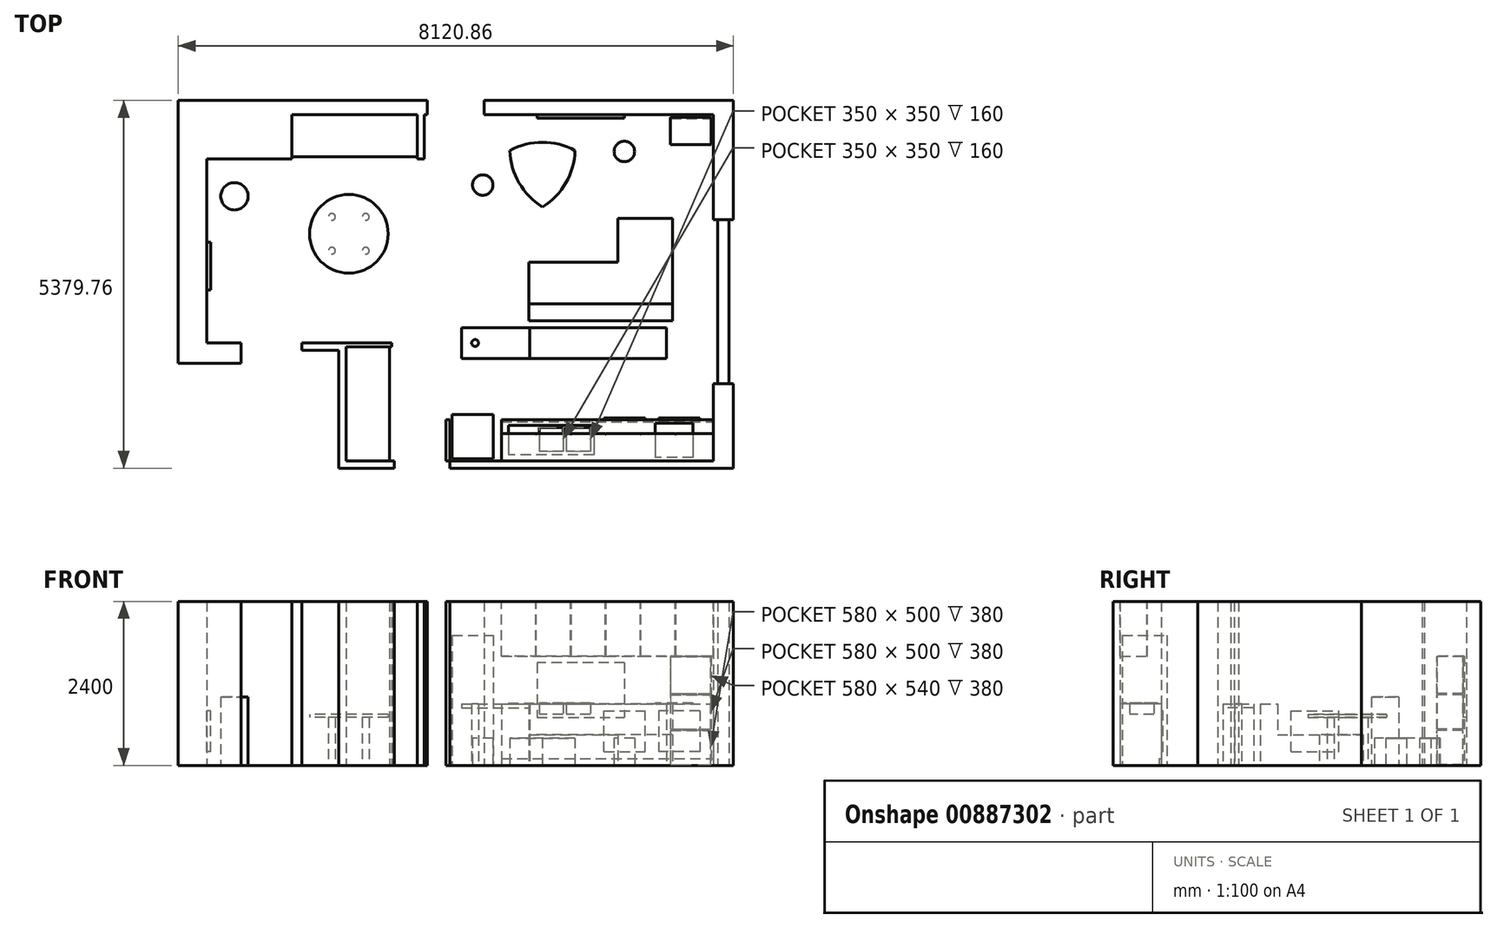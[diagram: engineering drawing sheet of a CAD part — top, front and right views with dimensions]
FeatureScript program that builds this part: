
annotation { "Feature Type Name" : "Feature", "Feature Type Description" : "" }
export const myFeature = defineFeature(function(context is Context, id is Id, definition is map)
    precondition{}
    {
        {
            var Q0;
            Q0=qCreatedBy(makeId("Top.planeOp"),FACE);
            var sketch = newSketch(context, id + "F0", { "sketchPlane" : qUnion([Q0])});
            skLineSegment(sketch, "E0", {"start": v(5332.87, -822.17) * mm, "end": v(1474.75, -822.17) * mm});
            skLineSegment(sketch, "E1", {"start": v(1474.75, -822.17) * mm, "end": v(1474.75, -222.17) * mm});
            skLineSegment(sketch, "E2", {"start": v(1474.75, -222.17) * mm, "end": v(1421.4, -222.17) * mm});
            skLineSegment(sketch, "E3", {"start": v(1421.4, -222.17) * mm, "end": v(1421.4, -822.17) * mm});
            skLineSegment(sketch, "E4", {"start": v(1421.4, -822.17) * mm, "end": v(1474.75, -822.17) * mm});
            skLineSegment(sketch, "E5", {"start": v(5332.87, 309.99) * mm, "end": v(5394.44, 309.99) * mm});
            skLineSegment(sketch, "E6", {"start": v(5394.44, 309.99) * mm, "end": v(5394.44, 2704.75) * mm});
            skLineSegment(sketch, "E7", {"start": v(5394.44, 2704.75) * mm, "end": v(5332.87, 2704.75) * mm});
            skLineSegment(sketch, "E8", {"start": v(5332.87, 2704.75) * mm, "end": v(5332.87, 4243.63) * mm});
            skLineSegment(sketch, "E9", {"start": v(5332.87, 4243.63) * mm, "end": v(1981.19, 4243.63) * mm});
            skLineSegment(sketch, "E10", {"start": v(1981.19, 4243.63) * mm, "end": v(1981.19, 4451) * mm});
            skLineSegment(sketch, "E11", {"start": v(1981.19, 4451) * mm, "end": v(5626.54, 4451) * mm});
            skLineSegment(sketch, "E12", {"start": v(5626.54, 4451) * mm, "end": v(5626.54, 2704.75) * mm});
            skLineSegment(sketch, "E13", {"start": v(5626.54, 2704.75) * mm, "end": v(5394.44, 2704.75) * mm});
            skLineSegment(sketch, "E14", {"start": v(5394.44, 309.99) * mm, "end": v(5626.54, 309.99) * mm});
            skPoint(sketch, "E14.endSnap0", {"position": v(5363.66, 309.99) * mm});
            skLineSegment(sketch, "E15", {"start": v(5626.54, 309.99) * mm, "end": v(5626.54, -928.77) * mm});
            skLineSegment(sketch, "E16", {"start": v(5626.54, -928.77) * mm, "end": v(1474.75, -928.77) * mm});
            skLineSegment(sketch, "E17", {"start": v(1474.75, -928.77) * mm, "end": v(1474.75, -822.17) * mm});
            skLineSegment(sketch, "E18", {"start": v(5558.56, 2704.75) * mm, "end": v(5558.56, 309.99) * mm});
            skLineSegment(sketch, "E19", {"start": v(-37.13, -822.17) * mm, "end": v(664.8, -822.17) * mm});
            skLineSegment(sketch, "E20", {"start": v(664.8, -822.17) * mm, "end": v(664.8, -928.77) * mm});
            skLineSegment(sketch, "E21", {"start": v(664.8, -928.77) * mm, "end": v(-150.57, -928.77) * mm});
            skLineSegment(sketch, "E22", {"start": v(-150.57, -928.77) * mm, "end": v(-150.57, 905.53) * mm});
            skLineSegment(sketch, "E23", {"start": v(-150.57, 905.53) * mm, "end": v(-37.13, 905.53) * mm});
            skLineSegment(sketch, "E24", {"start": v(-37.13, 905.53) * mm, "end": v(-37.13, -26.35) * mm});
            skLineSegment(sketch, "E25", {"start": v(5332.87, 309.99) * mm, "end": v(5332.87, -822.17) * mm});
            skLineSegment(sketch, "E26", {"start": v(-37.13, 905.53) * mm, "end": v(-37.13, -822.17) * mm});
            skLineSegment(sketch, "E27.bottom", {"start": v(1511.94, -792.17) * mm, "end": v(2111.94, -792.17) * mm});
            skLineSegment(sketch, "E27.left", {"start": v(1511.94, -792.17) * mm, "end": v(1511.94, -142.17) * mm});
            skLineSegment(sketch, "E28", {"start": v(1511.94, -142.17) * mm, "end": v(2111.94, -142.17) * mm});
            skLineSegment(sketch, "E29", {"start": v(2111.94, -142.17) * mm, "end": v(2111.94, -792.17) * mm});
            skLineSegment(sketch, "E30", {"start": v(5332.87, -822.17) * mm, "end": v(2232.87, -822.17) * mm, "construction": true});
            skLineSegment(sketch, "E31", {"start": v(2232.87, -822.17) * mm, "end": v(2232.87, -222.17) * mm});
            skLineSegment(sketch, "E32", {"start": v(5332.87, 309.99) * mm, "end": v(4732.87, 309.99) * mm, "construction": true});
            skLineSegment(sketch, "E33", {"start": v(2232.87, -222.17) * mm, "end": v(4732.87, -222.17) * mm});
            skLineSegment(sketch, "E34", {"start": v(4732.87, -222.17) * mm, "end": v(4732.87, 309.99) * mm, "construction": true});
            skLineSegment(sketch, "E35", {"start": v(1647.48, 677.83) * mm, "end": v(4647.48, 677.83) * mm});
            skLineSegment(sketch, "E36", {"start": v(4647.48, 677.83) * mm, "end": v(4647.48, 1127.83) * mm});
            skLineSegment(sketch, "E37", {"start": v(4647.48, 1127.83) * mm, "end": v(1647.48, 1127.83) * mm});
            skLineSegment(sketch, "E38", {"start": v(1647.48, 1127.83) * mm, "end": v(1647.48, 677.83) * mm, "construction": true});
            skLineSegment(sketch, "E39", {"start": v(4732.87, 1227.83) * mm, "end": v(2632.87, 1227.83) * mm});
            skLineSegment(sketch, "E40", {"start": v(2632.87, 1227.83) * mm, "end": v(2632.87, 2087.83) * mm});
            skLineSegment(sketch, "E41", {"start": v(2632.87, 2087.83) * mm, "end": v(3932.87, 2087.83) * mm});
            skLineSegment(sketch, "E42", {"start": v(4732.87, 1227.83) * mm, "end": v(4732.87, 2727.83) * mm});
            skLineSegment(sketch, "E43", {"start": v(4732.87, 2727.83) * mm, "end": v(3932.87, 2727.83) * mm});
            skLineSegment(sketch, "E44", {"start": v(3932.87, 2727.83) * mm, "end": v(3932.87, 2087.83) * mm});
            skLineSegment(sketch, "E45", {"start": v(4732.87, 1227.83) * mm, "end": v(4732.87, 1477.83) * mm, "construction": true});
            skLineSegment(sketch, "E46", {"start": v(4732.87, 1477.83) * mm, "end": v(2632.87, 1477.83) * mm});
            skLineSegment(sketch, "E47.bottom", {"start": v(5301.08, 4208.55) * mm, "end": v(4701.08, 4208.55) * mm});
            skLineSegment(sketch, "E47.top", {"start": v(5301.08, 3808.55) * mm, "end": v(4701.08, 3808.55) * mm});
            skLineSegment(sketch, "E47.left", {"start": v(5301.08, 4208.55) * mm, "end": v(5301.08, 3808.55) * mm});
            skLineSegment(sketch, "E47.right", {"start": v(4701.08, 4208.55) * mm, "end": v(4701.08, 3808.55) * mm});
            skLineSegment(sketch, "E48", {"start": v(4032.87, 4243.63) * mm, "end": v(4032.87, 4193.63) * mm});
            skLineSegment(sketch, "E49", {"start": v(4032.87, 4193.63) * mm, "end": v(2752.87, 4193.63) * mm});
            skLineSegment(sketch, "E50", {"start": v(2752.87, 4193.63) * mm, "end": v(2752.87, 4243.63) * mm});
            skLineSegment(sketch, "E51", {"start": v(2232.87, -549.5) * mm, "end": v(2332.87, -549.5) * mm, "construction": true});
            skLineSegment(sketch, "E52", {"start": v(2332.87, -302.17) * mm, "end": v(2332.87, -732.17) * mm});
            skLineSegment(sketch, "E53", {"start": v(2332.87, -302.17) * mm, "end": v(3582.87, -302.17) * mm});
            skLineSegment(sketch, "E54", {"start": v(3582.87, -302.17) * mm, "end": v(3582.87, -732.17) * mm});
            skLineSegment(sketch, "E55", {"start": v(3582.87, -732.17) * mm, "end": v(2332.87, -732.17) * mm});
            skLineSegment(sketch, "E56", {"start": v(3582.87, -517.17) * mm, "end": v(3532.87, -517.17) * mm, "construction": true});
            skLineSegment(sketch, "E57", {"start": v(3532.87, -517.17) * mm, "end": v(3182.87, -517.17) * mm, "construction": true});
            skLineSegment(sketch, "E58", {"start": v(3182.87, -517.17) * mm, "end": v(3132.87, -517.17) * mm, "construction": true});
            skLineSegment(sketch, "E59", {"start": v(3132.87, -517.17) * mm, "end": v(2782.87, -517.17) * mm, "construction": true});
            skLineSegment(sketch, "E60", {"start": v(3352.05, -302.17) * mm, "end": v(3352.05, -332.17) * mm, "construction": true});
            skLineSegment(sketch, "E61", {"start": v(3352.05, -332.17) * mm, "end": v(3352.05, -682.17) * mm, "construction": true});
            skLineSegment(sketch, "E62.bottom", {"start": v(3532.87, -332.17) * mm, "end": v(3182.87, -332.17) * mm});
            skLineSegment(sketch, "E62.top", {"start": v(3532.87, -682.17) * mm, "end": v(3182.87, -682.17) * mm});
            skLineSegment(sketch, "E62.left", {"start": v(3532.87, -332.17) * mm, "end": v(3532.87, -682.17) * mm});
            skLineSegment(sketch, "E62.right", {"start": v(3182.87, -332.17) * mm, "end": v(3182.87, -682.17) * mm});
            skLineSegment(sketch, "E63.bottom", {"start": v(3132.87, -332.17) * mm, "end": v(2782.87, -332.17) * mm});
            skLineSegment(sketch, "E63.top", {"start": v(3132.87, -682.17) * mm, "end": v(2782.87, -682.17) * mm});
            skLineSegment(sketch, "E63.left", {"start": v(3132.87, -332.17) * mm, "end": v(3132.87, -682.17) * mm});
            skLineSegment(sketch, "E63.right", {"start": v(2782.87, -332.17) * mm, "end": v(2782.87, -682.17) * mm});
            skLineSegment(sketch, "E64.bottom", {"start": v(5032.87, -272.17) * mm, "end": v(4482.87, -272.17) * mm});
            skLineSegment(sketch, "E64.top", {"start": v(5032.87, -772.17) * mm, "end": v(4482.87, -772.17) * mm});
            skLineSegment(sketch, "E64.left", {"start": v(5032.87, -272.17) * mm, "end": v(5032.87, -772.17) * mm});
            skLineSegment(sketch, "E64.right", {"start": v(4482.87, -272.17) * mm, "end": v(4482.87, -772.17) * mm});
            skLineSegment(sketch, "E65", {"start": v(1647.48, 677.83) * mm, "end": v(2647.48, 677.83) * mm, "construction": true});
            skLineSegment(sketch, "E66", {"start": v(2647.48, 677.83) * mm, "end": v(2647.48, 1127.83) * mm});
            skLineSegment(sketch, "E67", {"start": v(2647.48, 902.83) * mm, "end": v(1847.48, 902.83) * mm, "construction": true});
            skCircle(sketch, "E68", {"center": v(1847.48, 902.83) * mm, "radius": 50 * mm});
            skLineSegment(sketch, "E69", {"start": v(5626.54, 309.99) * mm, "end": v(5626.54, -6920.01) * mm, "construction": true});
            skLineSegment(sketch, "E70", {"start": v(5626.54, -6920.01) * mm, "end": v(109096.54, -6920.01) * mm, "construction": true});
            skLineSegment(sketch, "E71", {"start": v(-150.57, 905.53) * mm, "end": v(-687.76, 905.53) * mm});
            skLineSegment(sketch, "E72", {"start": v(-687.76, 905.53) * mm, "end": v(-687.76, 793.16) * mm});
            skLineSegment(sketch, "E73", {"start": v(-687.76, 793.16) * mm, "end": v(-150.57, 793.16) * mm});
            skLineSegment(sketch, "E74", {"start": v(1145.44, 4243.63) * mm, "end": v(-834.24, 4243.63) * mm});
            skLineSegment(sketch, "E75", {"start": v(-834.24, 4243.63) * mm, "end": v(-834.24, 3594.84) * mm});
            skLineSegment(sketch, "E76", {"start": v(-834.24, 3594.84) * mm, "end": v(-2078.37, 3594.84) * mm});
            skLineSegment(sketch, "E77", {"start": v(-2078.37, 3594.84) * mm, "end": v(-2078.37, 905.53) * mm});
            skLineSegment(sketch, "E78", {"start": v(-2078.37, 905.53) * mm, "end": v(-1579.23, 905.53) * mm});
            skLineSegment(sketch, "E79", {"start": v(-1579.23, 905.53) * mm, "end": v(-1579.23, 605.3) * mm});
            skLineSegment(sketch, "E80", {"start": v(-1579.23, 605.3) * mm, "end": v(-2494.32, 605.3) * mm});
            skLineSegment(sketch, "E81", {"start": v(-2494.32, 605.3) * mm, "end": v(-2494.32, 4451) * mm});
            skLineSegment(sketch, "E82", {"start": v(-2494.32, 4451) * mm, "end": v(1145.44, 4451) * mm});
            skLineSegment(sketch, "E83", {"start": v(1145.44, 4451) * mm, "end": v(1145.44, 4243.63) * mm});
            skLineSegment(sketch, "E84", {"start": v(5332.87, 4243.63) * mm, "end": v(5332.87, 4451) * mm});
            skCircle(sketch, "E85", {"center": v(0, 2500.55) * mm, "radius": 350 * mm, "construction": true});
            skLineSegment(sketch, "E86", {"start": v(-247.49, 2748.03) * mm, "end": v(247.49, 2748.03) * mm, "construction": true});
            skLineSegment(sketch, "E87", {"start": v(247.49, 2748.03) * mm, "end": v(247.49, 2253.06) * mm, "construction": true});
            skLineSegment(sketch, "E88", {"start": v(247.49, 2253.06) * mm, "end": v(-247.49, 2253.06) * mm, "construction": true});
            skCircle(sketch, "E89", {"center": v(-247.49, 2748.03) * mm, "radius": 50 * mm});
            skCircle(sketch, "E90", {"center": v(247.49, 2748.03) * mm, "radius": 50 * mm});
            skCircle(sketch, "E91", {"center": v(247.49, 2253.06) * mm, "radius": 50 * mm});
            skCircle(sketch, "E92", {"center": v(-247.49, 2253.06) * mm, "radius": 50 * mm});
            skCircle(sketch, "E93", {"center": v(0, 2500.55) * mm, "radius": 575 * mm});
            skCircle(sketch, "E94", {"center": v(2832.87, 3443.63) * mm, "radius": 550 * mm, "construction": true});
            skLineSegment(sketch, "E95", {"start": v(2832.87, 3443.63) * mm, "end": v(2832.87, 2893.63) * mm, "construction": true});
            skArc(sketch, "E96", {"start": v(2832.87, 2893.63) * mm, "mid": v(3175.58, 3245.77) * mm, "end": v(3309.19, 3718.63) * mm});
            skArc(sketch, "E97", {"start": v(3309.19, 3718.63) * mm, "mid": v(2832.87, 3839.36) * mm, "end": v(2356.56, 3718.63) * mm});
            skArc(sketch, "E98", {"start": v(2356.56, 3718.63) * mm, "mid": v(2490.17, 3245.77) * mm, "end": v(2832.87, 2893.63) * mm});
            skLineSegment(sketch, "E99", {"start": v(2832.87, 3443.63) * mm, "end": v(3309.19, 3718.63) * mm, "construction": true});
            skLineSegment(sketch, "E100", {"start": v(2832.87, 3443.63) * mm, "end": v(2356.56, 3718.63) * mm, "construction": true});
            skLineSegment(sketch, "E101", {"start": v(3309.19, 3718.63) * mm, "end": v(2356.56, 3718.63) * mm, "construction": true});
            skLineSegment(sketch, "E102", {"start": v(2356.56, 3718.63) * mm, "end": v(2832.87, 2893.63) * mm, "construction": true});
            skLineSegment(sketch, "E103", {"start": v(2832.87, 2893.63) * mm, "end": v(3309.19, 3718.63) * mm, "construction": true});
            skCircle(sketch, "E104", {"center": v(4030.54, 3705.1) * mm, "radius": 150 * mm});
            skCircle(sketch, "E105", {"center": v(1959.1, 3213.96) * mm, "radius": 150 * mm});
            skLineSegment(sketch, "E106", {"start": v(4732.87, -222.17) * mm, "end": v(5332.87, -222.17) * mm});
            skLineSegment(sketch, "E107", {"start": v(1101.26, 4243.63) * mm, "end": v(1101.26, 3594.84) * mm});
            skLineSegment(sketch, "E108", {"start": v(1101.26, 3594.84) * mm, "end": v(1001.26, 3594.84) * mm});
            skLineSegment(sketch, "E109", {"start": v(1001.26, 3594.84) * mm, "end": v(1001.26, 4243.63) * mm});
            skLineSegment(sketch, "E110", {"start": v(1001.26, 3627.05) * mm, "end": v(-834.24, 3627.05) * mm});
            skLineSegment(sketch, "E111", {"start": v(597.97, -822.17) * mm, "end": v(597.97, 845.53) * mm});
            skLineSegment(sketch, "E112", {"start": v(597.97, 905.53) * mm, "end": v(624.1, 905.53) * mm});
            skLineSegment(sketch, "E113", {"start": v(624.1, 905.53) * mm, "end": v(624.1, 845.53) * mm});
            skLineSegment(sketch, "E114", {"start": v(624.1, 845.53) * mm, "end": v(-37.13, 845.53) * mm});
            skLineSegment(sketch, "E115", {"start": v(-37.13, 905.53) * mm, "end": v(597.97, 905.53) * mm});
            skCircle(sketch, "E116", {"center": v(-1673.98, 3049.9) * mm, "radius": 200 * mm});
            skSolve(sketch);
        }
        {
            var Q0;
            {var subQ3=sQuery(id+"F0.wireOp",EDGE,"E7");Q0=makeQuery(id+"F0.imprint","IMPRINT",FACE,{"disambiguationData":[TD([[makeQuery(id+"F0.imprint","IMPRINT",EDGE,{"derivedFrom":subQ3}),-1.0]])]});}
            var Q1;
            {var subQ1=sQuery(id+"F0.wireOp",EDGE,"E5");Q1=makeQuery(id+"F0.imprint","IMPRINT",FACE,{"disambiguationData":[TD([[makeQuery(id+"F0.imprint","IMPRINT",EDGE,{"derivedFrom":subQ1}),-1.0]])]});}
            var Q2;
            {var subQ1=sQuery(id+"F0.wireOp",EDGE,"E20");Q2=makeQuery(id+"F0.imprint","IMPRINT",FACE,{"disambiguationData":[TD([[makeQuery(id+"F0.imprint","IMPRINT",EDGE,{"derivedFrom":subQ1}),-1.0]])]});}
            var Q3;
            Q3=makeQuery(id+"F0.imprint","IMPRINT",FACE,{"disambiguationData":[TD([[makeQuery(id+"F0.imprint","IMPRINT",EDGE,{"derivedFrom":sQuery(id+"F0.wireOp",EDGE,"E1")}),1.0]])]});
            var Q4;
            {var subQ0=sQuery(id+"F0.wireOp",EDGE,"E76");Q4=makeQuery(id+"F0.imprint","IMPRINT",FACE,{"disambiguationData":[TD([[makeQuery(id+"F0.imprint","IMPRINT",EDGE,{"derivedFrom":subQ0}),-1.0]])]});}
            var Q5;
            {var subQ0=sQuery(id+"F0.wireOp",EDGE,"E71");Q5=makeQuery(id+"F0.imprint","IMPRINT",FACE,{"disambiguationData":[TD([[makeQuery(id+"F0.imprint","IMPRINT",EDGE,{"derivedFrom":subQ0}),1.0]])]});}
            var Q6;
            {var subQ0=sQuery(id+"F0.wireOp",EDGE,"E10");Q6=makeQuery(id+"F0.imprint","IMPRINT",FACE,{"disambiguationData":[TD([[makeQuery(id+"F0.imprint","IMPRINT",EDGE,{"derivedFrom":subQ0}),-1.0]])]});}
            var Q7;
            {var subQ4=sQuery(id+"F0.wireOp",EDGE,"E107");Q7=makeQuery(id+"F0.imprint","IMPRINT",FACE,{"disambiguationData":[TD([[makeQuery(id+"F0.imprint","IMPRINT",EDGE,{"derivedFrom":subQ4}),-1.0]])]});}
            var Q8;
            Q8=makeQuery(id+"F0.imprint","IMPRINT",FACE,{"disambiguationData":[TD([[makeQuery(id+"F0.imprint","IMPRINT",EDGE,{"derivedFrom":sQuery(id+"F0.wireOp",EDGE,"E112")}),-1.0]])]});
            extrude(context, id + "F1", {"entities" : qUnion([Q0, Q1, Q2, Q3, Q4, Q5, Q6, Q7, Q8]), "depth" : 2400 * mm, "offsetDistance" : 25 * mm});
        }
        {
            var Q0;
            {var subQ3=sQuery(id+"F0.wireOp",EDGE,"E31");Q0=makeQuery(id+"F0.imprint","IMPRINT",FACE,{"disambiguationData":[TD([[makeQuery(id+"F0.imprint","IMPRINT",EDGE,{"derivedFrom":subQ3}),-1.0]])]});}
            var Q1;
            {var subQ2=sQuery(id+"F0.wireOp",EDGE,"E36");Q1=makeQuery(id+"F0.imprint","IMPRINT",FACE,{"disambiguationData":[TD([[makeQuery(id+"F0.imprint","IMPRINT",EDGE,{"derivedFrom":subQ2}),1.0]])]});}
            var Q2;
            Q2=makeQuery(id+"F0.imprint","IMPRINT",FACE,{"disambiguationData":[TD([[makeQuery(id+"F0.imprint","IMPRINT",EDGE,{"derivedFrom":sQuery(id+"F0.wireOp",EDGE,"E68")}),1.0]])]});
            extrude(context, id + "F2", {"entities" : qUnion([Q0, Q1, Q2]), "depth" : 900 * mm, "offsetDistance" : 25 * mm});
        }
        {
            var Q0;
            Q0=makeQuery(id+"F1.opExtrude","CAP_FACE",FACE,{"disambiguationData":[OSD([sQuery(id+"F0.wireOp",EDGE,"E0"),sQuery(id+"F0.wireOp",EDGE,"E5"),sQuery(id+"F0.wireOp",EDGE,"E14"),sQuery(id+"F0.wireOp",EDGE,"E15"),sQuery(id+"F0.wireOp",EDGE,"E16"),sQuery(id+"F0.wireOp",EDGE,"E17"),sQuery(id+"F0.wireOp",EDGE,"E25")])],"isStart":false});
            var sketch = newSketch(context, id + "F3", { "sketchPlane" : qUnion([Q0])});
            skLineSegment(sketch, "E117", {"start": v(5332.87, -822.17) * mm, "end": v(2232.87, -822.17) * mm});
            skLineSegment(sketch, "E118", {"start": v(2232.87, -822.17) * mm, "end": v(2232.87, -422.17) * mm});
            skLineSegment(sketch, "E119", {"start": v(2232.87, -422.17) * mm, "end": v(5332.87, -422.17) * mm});
            skLineSegment(sketch, "E120", {"start": v(5332.87, -422.17) * mm, "end": v(5332.87, -822.17) * mm});
            skSolve(sketch);
        }
        {
            var Q0;
            Q0=makeQuery(id+"F3.imprint","IMPRINT",FACE,{"disambiguationData":[TD([[makeQuery(id+"F3.imprint","IMPRINT",EDGE,{"derivedFrom":sQuery(id+"F3.wireOp",EDGE,"E117")}),-1.0]])]});
            extrude(context, id + "F4", {"entities" : qUnion([Q0]), "oppositeDirection" : true, "depth" : 800 * mm, "offsetDistance" : 25 * mm});
        }
        {
            var Q0;
            Q0=makeQuery(id+"F0.imprint","IMPRINT",FACE,{"disambiguationData":[TD([[makeQuery(id+"F0.imprint","IMPRINT",EDGE,{"derivedFrom":sQuery(id+"F0.wireOp",EDGE,"E27.bottom")}),1.0]])]});
            extrude(context, id + "F5", {"entities" : qUnion([Q0]), "depth" : 1900 * mm, "offsetDistance" : 25 * mm});
        }
        {
            var Q0;
            {var subQ0=sQuery(id+"F0.wireOp",EDGE,"E39");Q0=makeQuery(id+"F0.imprint","IMPRINT",FACE,{"disambiguationData":[TD([[makeQuery(id+"F0.imprint","IMPRINT",EDGE,{"derivedFrom":subQ0}),-1.0]])]});}
            extrude(context, id + "F6", {"entities" : qUnion([Q0]), "depth" : 900 * mm, "offsetDistance" : 25 * mm});
        }
        {
            var Q0;
            {var subQ3=sQuery(id+"F0.wireOp",EDGE,"E41");Q0=makeQuery(id+"F0.imprint","IMPRINT",FACE,{"disambiguationData":[TD([[makeQuery(id+"F0.imprint","IMPRINT",EDGE,{"derivedFrom":subQ3}),-1.0]])]});}
            extrude(context, id + "F7", {"entities" : qUnion([Q0]), "operationType" : NewBodyOperationType.ADD, "depth" : 450 * mm, "offsetDistance" : 25 * mm});
        }
        {
            var Q0;
            Q0=makeQuery(id+"F0.imprint","IMPRINT",FACE,{"disambiguationData":[TD([[makeQuery(id+"F0.imprint","IMPRINT",EDGE,{"derivedFrom":sQuery(id+"F0.wireOp",EDGE,"E52")}),1.0]])]});
            extrude(context, id + "F8", {"entities" : qUnion([Q0]), "operationType" : NewBodyOperationType.ADD, "depth" : 910 * mm, "offsetDistance" : 25 * mm});
        }
        {
            var Q0;
            Q0=makeQuery(id+"F0.imprint","IMPRINT",FACE,{"disambiguationData":[TD([[makeQuery(id+"F0.imprint","IMPRINT",EDGE,{"derivedFrom":sQuery(id+"F0.wireOp",EDGE,"E62.bottom")}),1.0]])]});
            var Q1;
            Q1=makeQuery(id+"F0.imprint","IMPRINT",FACE,{"disambiguationData":[TD([[makeQuery(id+"F0.imprint","IMPRINT",EDGE,{"derivedFrom":sQuery(id+"F0.wireOp",EDGE,"E63.bottom")}),1.0]])]});
            extrude(context, id + "F9", {"entities" : qUnion([Q0, Q1]), "operationType" : NewBodyOperationType.ADD, "depth" : 750 * mm, "offsetDistance" : 25 * mm});
        }
        {
            var Q0;
            Q0=makeQuery(id+"F0.imprint","IMPRINT",FACE,{"disambiguationData":[TD([[makeQuery(id+"F0.imprint","IMPRINT",EDGE,{"derivedFrom":sQuery(id+"F0.wireOp",EDGE,"E64.bottom")}),1.0]])]});
            extrude(context, id + "F10", {"entities" : qUnion([Q0]), "operationType" : NewBodyOperationType.ADD, "depth" : 910 * mm, "offsetDistance" : 25 * mm});
        }
        {
            var Q0;
            Q0=makeQuery(id+"F2.opExtrude","SWEPT_FACE",FACE,{"disambiguationData":[OSD([sQuery(id+"F0.wireOp",EDGE,"E66")])]});
            var sketch = newSketch(context, id + "F11", { "sketchPlane" : qUnion([Q0])});
            skLineSegment(sketch, "E121.bottom", {"start": v(-1127.83, 900) * mm, "end": v(-527.83, 900) * mm});
            skLineSegment(sketch, "E121.top", {"start": v(-1127.83, 840) * mm, "end": v(-527.83, 840) * mm});
            skLineSegment(sketch, "E121.left", {"start": v(-1127.83, 900) * mm, "end": v(-1127.83, 840) * mm});
            skLineSegment(sketch, "E121.right", {"start": v(-527.83, 900) * mm, "end": v(-527.83, 840) * mm});
            skSolve(sketch);
        }
        {
            var Q0;
            Q0=makeQuery(id+"F11.imprint","IMPRINT",FACE,{"disambiguationData":[TD([[makeQuery(id+"F11.imprint","IMPRINT",EDGE,{"derivedFrom":sQuery(id+"F11.wireOp",EDGE,"E121.bottom")}),1.0]])]});
            extrude(context, id + "F12", {"entities" : qUnion([Q0]), "depth" : 1000 * mm, "offsetDistance" : 25 * mm});
        }
        {
            var Q0;
            {var subQ0=sQuery(id+"F0.wireOp",EDGE,"E6");Q0=makeQuery(id+"F0.imprint","IMPRINT",FACE,{"disambiguationData":[TD([[makeQuery(id+"F0.imprint","IMPRINT",EDGE,{"derivedFrom":subQ0}),-1.0]])]});}
            extrude(context, id + "F13", {"entities" : qUnion([Q0]), "depth" : 2400 * mm, "offsetDistance" : 25 * mm});
        }
        {
            var Q0;
            Q0=makeQuery(id+"F0.imprint","IMPRINT",FACE,{"disambiguationData":[TD([[makeQuery(id+"F0.imprint","IMPRINT",EDGE,{"derivedFrom":sQuery(id+"F0.wireOp",EDGE,"E89")}),-1.0]])]});
            var Q1;
            Q1=makeQuery(id+"Fm7Inrb7nq87sZd_8.opExtrude","CAP_FACE",FACE,{"disambiguationData":[OSD([sQuery(id+"F0.wireOp",EDGE,"E90")])],"isStart":false});
            var Q2;
            Q2=makeQuery(id+"Fm7Inrb7nq87sZd_8.opExtrude","CAP_FACE",FACE,{"disambiguationData":[OSD([sQuery(id+"F0.wireOp",EDGE,"E91")])],"isStart":false});
            var Q3;
            Q3=makeQuery(id+"Fm7Inrb7nq87sZd_8.opExtrude","CAP_FACE",FACE,{"disambiguationData":[OSD([sQuery(id+"F0.wireOp",EDGE,"E89")])],"isStart":false});
            var Q4;
            Q4=makeQuery(id+"Fm7Inrb7nq87sZd_8.opExtrude","CAP_FACE",FACE,{"disambiguationData":[OSD([sQuery(id+"F0.wireOp",EDGE,"E92")])],"isStart":false});
            var Q5;
            Q5=makeQuery(id+"F0.imprint","IMPRINT",FACE,{"disambiguationData":[TD([[makeQuery(id+"F0.imprint","IMPRINT",EDGE,{"derivedFrom":sQuery(id+"F0.wireOp",EDGE,"E90")}),1.0]])]});
            var Q6;
            Q6=makeQuery(id+"F0.imprint","IMPRINT",FACE,{"disambiguationData":[TD([[makeQuery(id+"F0.imprint","IMPRINT",EDGE,{"derivedFrom":sQuery(id+"F0.wireOp",EDGE,"E91")}),1.0]])]});
            var Q7;
            Q7=makeQuery(id+"F0.imprint","IMPRINT",FACE,{"disambiguationData":[TD([[makeQuery(id+"F0.imprint","IMPRINT",EDGE,{"derivedFrom":sQuery(id+"F0.wireOp",EDGE,"E89")}),1.0]])]});
            var Q8;
            Q8=makeQuery(id+"F0.imprint","IMPRINT",FACE,{"disambiguationData":[TD([[makeQuery(id+"F0.imprint","IMPRINT",EDGE,{"derivedFrom":sQuery(id+"F0.wireOp",EDGE,"E92")}),1.0]])]});
            extrude(context, id + "F14", {"entities" : qUnion([Q0, Q1, Q2, Q3, Q4, Q5, Q6, Q7, Q8]), "depth" : 750 * mm, "offsetDistance" : 25 * mm});
        }
        {
            var Q0;
            Q0=makeQuery(id+"F0.imprint","IMPRINT",FACE,{"disambiguationData":[TD([[makeQuery(id+"F0.imprint","IMPRINT",EDGE,{"derivedFrom":sQuery(id+"F0.wireOp",EDGE,"E89")}),-1.0]])]});
            extrude(context, id + "F15", {"entities" : qUnion([Q0]), "depth" : 700 * mm, "offsetDistance" : 25 * mm});
        }
        {
            var Q0;
            Q0=makeQuery(id+"F15.opExtrude","SWEPT_BODY",BODY,{"disambiguationData":[OSD([sQuery(id+"F0.wireOp",EDGE,"E89"),sQuery(id+"F0.wireOp",EDGE,"E90"),sQuery(id+"F0.wireOp",EDGE,"E91"),sQuery(id+"F0.wireOp",EDGE,"E92"),sQuery(id+"F0.wireOp",EDGE,"E93")])]});
            var Q1;
            Q1=makeQuery(id+"F14.opExtrude","SWEPT_BODY",BODY,{"disambiguationData":[OSD([sQuery(id+"F0.wireOp",EDGE,"E93")])]});
            booleanBodies(context, id + "F16", {"operationType" : BooleanOperationType.SUBTRACTION, "tools" : qUnion([Q0]), "targets" : qUnion([Q1])});
        }
        {
            var Q0;
            {var subQ0=sQuery(id+"F0.wireOp",EDGE,"E48");Q0=makeQuery(id+"F0.imprint","IMPRINT",FACE,{"disambiguationData":[TD([[makeQuery(id+"F0.imprint","IMPRINT",EDGE,{"derivedFrom":subQ0}),-1.0]])]});}
            extrude(context, id + "F17", {"entities" : qUnion([Q0]), "depth" : 1500 * mm, "offsetDistance" : 25 * mm});
        }
        {
            var Q0;
            Q0=makeQuery(id+"F17.opExtrude","SWEPT_FACE",FACE,{"disambiguationData":[OSD([sQuery(id+"F0.wireOp",EDGE,"E49")])]});
            var sketch = newSketch(context, id + "F18", { "sketchPlane" : qUnion([Q0])});
            skLineSegment(sketch, "E122.bottom", {"start": v(2752.87, 0) * mm, "end": v(4032.87, 0) * mm});
            skLineSegment(sketch, "E122.top", {"start": v(2752.87, 700) * mm, "end": v(4032.87, 700) * mm});
            skLineSegment(sketch, "E122.left", {"start": v(2752.87, 0) * mm, "end": v(2752.87, 700) * mm});
            skLineSegment(sketch, "E122.right", {"start": v(4032.87, 0) * mm, "end": v(4032.87, 700) * mm});
            skSolve(sketch);
        }
        {
            var Q0;
            Q0=makeQuery(id+"F18.imprint","IMPRINT",FACE,{"disambiguationData":[TD([[makeQuery(id+"F18.imprint","IMPRINT",EDGE,{"derivedFrom":sQuery(id+"F18.wireOp",EDGE,"E122.bottom")}),-1.0]])]});
            extrude(context, id + "F19", {"entities" : qUnion([Q0]), "operationType" : NewBodyOperationType.REMOVE, "oppositeDirection" : true, "depth" : 50 * mm, "offsetDistance" : 25 * mm});
        }
        {
            var Q0;
            Q0=makeQuery(id+"F0.imprint","IMPRINT",FACE,{"disambiguationData":[TD([[makeQuery(id+"F0.imprint","IMPRINT",EDGE,{"derivedFrom":sQuery(id+"F0.wireOp",EDGE,"E96")}),1.0]])]});
            var Q1;
            Q1=makeQuery(id+"F0.imprint","IMPRINT",FACE,{"disambiguationData":[TD([[makeQuery(id+"F0.imprint","IMPRINT",EDGE,{"derivedFrom":sQuery(id+"F0.wireOp",EDGE,"E104")}),1.0]])]});
            var Q2;
            Q2=makeQuery(id+"F0.imprint","IMPRINT",FACE,{"disambiguationData":[TD([[makeQuery(id+"F0.imprint","IMPRINT",EDGE,{"derivedFrom":sQuery(id+"F0.wireOp",EDGE,"E105")}),1.0]])]});
            extrude(context, id + "F20", {"entities" : qUnion([Q0, Q1, Q2]), "depth" : 400 * mm, "offsetDistance" : 25 * mm});
        }
        {
            var Q0;
            Q0=makeQuery(id+"F0.imprint","IMPRINT",FACE,{"disambiguationData":[TD([[makeQuery(id+"F0.imprint","IMPRINT",EDGE,{"derivedFrom":sQuery(id+"F0.wireOp",EDGE,"E47.bottom")}),1.0]])]});
            extrude(context, id + "F21", {"entities" : qUnion([Q0]), "depth" : 1600 * mm, "offsetDistance" : 25 * mm});
        }
        {
            var Q0;
            Q0=makeQuery(id+"F21.opExtrude","SWEPT_FACE",FACE,{"disambiguationData":[OSD([sQuery(id+"F0.wireOp",EDGE,"E47.top")])]});
            var sketch = newSketch(context, id + "F22", { "sketchPlane" : qUnion([Q0])});
            skCircle(sketch, "E123", {"center": v(4701.08, 1600) * mm, "radius": 10 * mm, "construction": true});
            skCircle(sketch, "E124", {"center": v(5301.08, 1600) * mm, "radius": 10 * mm, "construction": true});
            skLineSegment(sketch, "E125", {"start": v(4701.08, 1590) * mm, "end": v(5301.08, 1590) * mm, "construction": true});
            skCircle(sketch, "E126", {"center": v(4701.08, 0) * mm, "radius": 10 * mm, "construction": true});
            skCircle(sketch, "E127", {"center": v(5301.08, 0) * mm, "radius": 10 * mm, "construction": true});
            skLineSegment(sketch, "E128", {"start": v(5301.08, 10) * mm, "end": v(4701.08, 10) * mm, "construction": true});
            skLineSegment(sketch, "E129", {"start": v(4711.08, 0) * mm, "end": v(4711.08, 10) * mm, "construction": true});
            skLineSegment(sketch, "E130", {"start": v(5291.08, 0) * mm, "end": v(5291.08, 10) * mm, "construction": true});
            skLineSegment(sketch, "E131", {"start": v(4711.08, 1600) * mm, "end": v(4711.08, 1590) * mm, "construction": true});
            skLineSegment(sketch, "E132.bottom", {"start": v(4711.08, 1590) * mm, "end": v(5291.08, 1590) * mm, "construction": true});
            skLineSegment(sketch, "E132.top", {"start": v(4711.08, 10) * mm, "end": v(5291.08, 10) * mm, "construction": true});
            skLineSegment(sketch, "E132.left", {"start": v(4711.08, 1590) * mm, "end": v(4711.08, 10) * mm, "construction": true});
            skLineSegment(sketch, "E132.right", {"start": v(5291.08, 1590) * mm, "end": v(5291.08, 10) * mm, "construction": true});
            skLineSegment(sketch, "E133.bottom", {"start": v(4711.08, 10) * mm, "end": v(5291.08, 10) * mm});
            skLineSegment(sketch, "E133.top", {"start": v(4711.08, 510) * mm, "end": v(5291.08, 510) * mm});
            skLineSegment(sketch, "E133.left", {"start": v(4711.08, 10) * mm, "end": v(4711.08, 510) * mm});
            skLineSegment(sketch, "E133.right", {"start": v(5291.08, 10) * mm, "end": v(5291.08, 510) * mm});
            skLineSegment(sketch, "E134", {"start": v(4711.08, 510) * mm, "end": v(4711.08, 530) * mm, "construction": true});
            skLineSegment(sketch, "E135.bottom", {"start": v(4711.08, 530) * mm, "end": v(5291.08, 530) * mm});
            skLineSegment(sketch, "E135.top", {"start": v(4711.08, 1030) * mm, "end": v(5291.08, 1030) * mm});
            skLineSegment(sketch, "E135.left", {"start": v(4711.08, 530) * mm, "end": v(4711.08, 1030) * mm});
            skLineSegment(sketch, "E135.right", {"start": v(5291.08, 530) * mm, "end": v(5291.08, 1030) * mm});
            skLineSegment(sketch, "E136", {"start": v(4711.08, 1030) * mm, "end": v(4711.08, 1050) * mm, "construction": true});
            skLineSegment(sketch, "E137.bottom", {"start": v(4711.08, 1050) * mm, "end": v(5291.08, 1050) * mm});
            skLineSegment(sketch, "E137.top", {"start": v(4711.08, 1590) * mm, "end": v(5291.08, 1590) * mm});
            skLineSegment(sketch, "E137.left", {"start": v(4711.08, 1050) * mm, "end": v(4711.08, 1590) * mm});
            skLineSegment(sketch, "E137.right", {"start": v(5291.08, 1050) * mm, "end": v(5291.08, 1590) * mm});
            skSolve(sketch);
        }
        {
            var Q0;
            Q0=makeQuery(id+"F22.imprint","IMPRINT",FACE,{"disambiguationData":[TD([[makeQuery(id+"F22.imprint","IMPRINT",EDGE,{"derivedFrom":sQuery(id+"F22.wireOp",EDGE,"E137.bottom")}),1.0]])]});
            var Q1;
            Q1=makeQuery(id+"F22.imprint","IMPRINT",FACE,{"disambiguationData":[TD([[makeQuery(id+"F22.imprint","IMPRINT",EDGE,{"derivedFrom":sQuery(id+"F22.wireOp",EDGE,"E135.bottom")}),1.0]])]});
            var Q2;
            Q2=makeQuery(id+"F22.imprint","IMPRINT",FACE,{"disambiguationData":[TD([[makeQuery(id+"F22.imprint","IMPRINT",EDGE,{"derivedFrom":sQuery(id+"F22.wireOp",EDGE,"E133.bottom")}),1.0]])]});
            extrude(context, id + "F23", {"entities" : qUnion([Q0, Q1, Q2]), "operationType" : NewBodyOperationType.REMOVE, "oppositeDirection" : true, "depth" : 380 * mm, "offsetDistance" : 25 * mm});
        }
        {
            var Q0;
            Q0=makeQuery(id+"F2.opExtrude","SWEPT_FACE",FACE,{"disambiguationData":[OSD([sQuery(id+"F0.wireOp",EDGE,"E33"),sQuery(id+"F0.wireOp",EDGE,"E106")])]});
            var sketch = newSketch(context, id + "F24", { "sketchPlane" : qUnion([Q0])});
            skLineSegment(sketch, "E138", {"start": v(-2232.87, 100) * mm, "end": v(-2232.87, 100) * mm});
            skLineSegment(sketch, "E139.bottom", {"start": v(-3732.87, 200) * mm, "end": v(-4332.87, 200) * mm});
            skLineSegment(sketch, "E139.top", {"start": v(-3732.87, 800) * mm, "end": v(-4332.87, 800) * mm});
            skLineSegment(sketch, "E139.left", {"start": v(-3732.87, 200) * mm, "end": v(-3732.87, 800) * mm});
            skLineSegment(sketch, "E139.right", {"start": v(-4332.87, 200) * mm, "end": v(-4332.87, 800) * mm});
            skLineSegment(sketch, "E140", {"start": v(-2232.87, 900) * mm, "end": v(-2232.87, 0) * mm, "construction": true});
            skLineSegment(sketch, "E141.bottom", {"start": v(-5132.87, 800) * mm, "end": v(-4532.87, 800) * mm});
            skLineSegment(sketch, "E141.top", {"start": v(-5132.87, 200) * mm, "end": v(-4532.87, 200) * mm});
            skLineSegment(sketch, "E141.left", {"start": v(-5132.87, 800) * mm, "end": v(-5132.87, 200) * mm});
            skLineSegment(sketch, "E141.right", {"start": v(-4532.87, 800) * mm, "end": v(-4532.87, 200) * mm});
            skLineSegment(sketch, "E142", {"start": v(-2232.87, 100) * mm, "end": v(-5332.87, 100) * mm});
            skSolve(sketch);
        }
        {
            var Q0;
            Q0=makeQuery(id+"F24.imprint","IMPRINT",FACE,{"disambiguationData":[TD([[makeQuery(id+"F24.imprint","IMPRINT",EDGE,{"derivedFrom":sQuery(id+"F24.wireOp",EDGE,"E141.bottom")}),-1.0]])]});
            var Q1;
            Q1=makeQuery(id+"F24.imprint","IMPRINT",FACE,{"disambiguationData":[TD([[makeQuery(id+"F24.imprint","IMPRINT",EDGE,{"derivedFrom":sQuery(id+"F24.wireOp",EDGE,"E139.bottom")}),-1.0]])]});
            extrude(context, id + "F25", {"entities" : qUnion([Q0, Q1]), "operationType" : NewBodyOperationType.ADD, "depth" : 25 * mm, "offsetDistance" : 25 * mm});
        }
        {
            var Q0;
            {var subQ0=sQuery(id+"F24.wireOp",EDGE,"E142");Q0=makeQuery(id+"F24.imprint","IMPRINT",FACE,{"disambiguationData":[TD([[makeQuery(id+"F24.imprint","IMPRINT",EDGE,{"derivedFrom":subQ0}),1.0]])]});}
            extrude(context, id + "F26", {"entities" : qUnion([Q0]), "operationType" : NewBodyOperationType.REMOVE, "oppositeDirection" : true, "depth" : 30 * mm, "offsetDistance" : 25 * mm});
        }
        {
            var Q0;
            Q0=makeQuery(id+"F4.opExtrude","SWEPT_FACE",FACE,{"disambiguationData":[OSD([sQuery(id+"F3.wireOp",EDGE,"E119")])]});
            var sketch = newSketch(context, id + "F27", { "sketchPlane" : qUnion([Q0])});
            skLineSegment(sketch, "E143", {"start": v(-5332.87, 1600) * mm, "end": v(-5332.87, 2400) * mm, "construction": true});
            skLineSegment(sketch, "E144", {"start": v(-2232.87, 1600) * mm, "end": v(-2732.87, 1600) * mm, "construction": true});
            skLineSegment(sketch, "E145.bottom", {"start": v(-2732.87, 1600) * mm, "end": v(-2742.87, 1600) * mm});
            skLineSegment(sketch, "E145.top", {"start": v(-2732.87, 2400) * mm, "end": v(-2742.87, 2400) * mm});
            skLineSegment(sketch, "E145.left", {"start": v(-2732.87, 1600) * mm, "end": v(-2732.87, 2400) * mm});
            skLineSegment(sketch, "E145.right", {"start": v(-2742.87, 1600) * mm, "end": v(-2742.87, 2400) * mm});
            skLineSegment(sketch, "E146", {"start": v(-2742.87, 1600) * mm, "end": v(-3242.87, 1600) * mm, "construction": true});
            skLineSegment(sketch, "E147", {"start": v(-3242.87, 1600) * mm, "end": v(-3752.87, 1600) * mm, "construction": true});
            skLineSegment(sketch, "E148", {"start": v(-3752.87, 1600) * mm, "end": v(-4262.87, 1600) * mm, "construction": true});
            skLineSegment(sketch, "E149", {"start": v(-4262.87, 1600) * mm, "end": v(-4772.87, 1600) * mm, "construction": true});
            skLineSegment(sketch, "E150.bottom", {"start": v(-3242.87, 1600) * mm, "end": v(-3252.87, 1600) * mm});
            skLineSegment(sketch, "E150.top", {"start": v(-3242.87, 2400) * mm, "end": v(-3252.87, 2400) * mm});
            skLineSegment(sketch, "E150.left", {"start": v(-3242.87, 1600) * mm, "end": v(-3242.87, 2400) * mm});
            skLineSegment(sketch, "E150.right", {"start": v(-3252.87, 1600) * mm, "end": v(-3252.87, 2400) * mm});
            skLineSegment(sketch, "E151.bottom", {"start": v(-3752.87, 1600) * mm, "end": v(-3762.87, 1600) * mm});
            skLineSegment(sketch, "E151.top", {"start": v(-3752.87, 2400) * mm, "end": v(-3762.87, 2400) * mm});
            skLineSegment(sketch, "E151.left", {"start": v(-3752.87, 1600) * mm, "end": v(-3752.87, 2400) * mm});
            skLineSegment(sketch, "E151.right", {"start": v(-3762.87, 1600) * mm, "end": v(-3762.87, 2400) * mm});
            skLineSegment(sketch, "E152.bottom", {"start": v(-4262.87, 1600) * mm, "end": v(-4272.87, 1600) * mm});
            skLineSegment(sketch, "E152.top", {"start": v(-4262.87, 2400) * mm, "end": v(-4272.87, 2400) * mm});
            skLineSegment(sketch, "E152.left", {"start": v(-4262.87, 1600) * mm, "end": v(-4262.87, 2400) * mm});
            skLineSegment(sketch, "E152.right", {"start": v(-4272.87, 1600) * mm, "end": v(-4272.87, 2400) * mm});
            skLineSegment(sketch, "E153.bottom", {"start": v(-4772.87, 1600) * mm, "end": v(-4782.87, 1600) * mm});
            skLineSegment(sketch, "E153.top", {"start": v(-4772.87, 2400) * mm, "end": v(-4782.87, 2400) * mm});
            skLineSegment(sketch, "E153.left", {"start": v(-4772.87, 1600) * mm, "end": v(-4772.87, 2400) * mm});
            skLineSegment(sketch, "E153.right", {"start": v(-4782.87, 1600) * mm, "end": v(-4782.87, 2400) * mm});
            skLineSegment(sketch, "E154", {"start": v(-4782.87, 1600) * mm, "end": v(-5282.87, 1600) * mm, "construction": true});
            skSolve(sketch);
        }
        {
            var Q0;
            Q0=makeQuery(id+"F27.imprint","IMPRINT",FACE,{"disambiguationData":[TD([[makeQuery(id+"F27.imprint","IMPRINT",EDGE,{"derivedFrom":sQuery(id+"F27.wireOp",EDGE,"E145.bottom")}),-1.0]])]});
            var Q1;
            Q1=makeQuery(id+"F27.imprint","IMPRINT",FACE,{"disambiguationData":[TD([[makeQuery(id+"F27.imprint","IMPRINT",EDGE,{"derivedFrom":sQuery(id+"F27.wireOp",EDGE,"E150.bottom")}),-1.0]])]});
            var Q2;
            Q2=makeQuery(id+"F27.imprint","IMPRINT",FACE,{"disambiguationData":[TD([[makeQuery(id+"F27.imprint","IMPRINT",EDGE,{"derivedFrom":sQuery(id+"F27.wireOp",EDGE,"E151.bottom")}),-1.0]])]});
            var Q3;
            Q3=makeQuery(id+"F27.imprint","IMPRINT",FACE,{"disambiguationData":[TD([[makeQuery(id+"F27.imprint","IMPRINT",EDGE,{"derivedFrom":sQuery(id+"F27.wireOp",EDGE,"E152.bottom")}),-1.0]])]});
            var Q4;
            Q4=makeQuery(id+"F27.imprint","IMPRINT",FACE,{"disambiguationData":[TD([[makeQuery(id+"F27.imprint","IMPRINT",EDGE,{"derivedFrom":sQuery(id+"F27.wireOp",EDGE,"E153.bottom")}),-1.0]])]});
            extrude(context, id + "F28", {"entities" : qUnion([Q0, Q1, Q2, Q3, Q4]), "operationType" : NewBodyOperationType.REMOVE, "oppositeDirection" : true, "depth" : 10 * mm, "offsetDistance" : 25 * mm});
        }
        {
            var Q0;
            Q0=makeQuery(id+"F1.opExtrude","SWEPT_FACE",FACE,{"disambiguationData":[OSD([sQuery(id+"F0.wireOp",EDGE,"E77")])]});
            var sketch = newSketch(context, id + "F29", { "sketchPlane" : qUnion([Q0])});
            skLineSegment(sketch, "E155.bottom", {"start": v(1676.7, 200) * mm, "end": v(2376.7, 200) * mm});
            skLineSegment(sketch, "E155.top", {"start": v(1676.7, 800) * mm, "end": v(2376.7, 800) * mm});
            skLineSegment(sketch, "E155.left", {"start": v(1676.7, 200) * mm, "end": v(1676.7, 800) * mm});
            skLineSegment(sketch, "E155.right", {"start": v(2376.7, 200) * mm, "end": v(2376.7, 800) * mm});
            skSolve(sketch);
        }
        {
            var Q0;
            Q0=makeQuery(id+"F29.imprint","IMPRINT",FACE,{"disambiguationData":[TD([[makeQuery(id+"F29.imprint","IMPRINT",EDGE,{"derivedFrom":sQuery(id+"F29.wireOp",EDGE,"E155.bottom")}),1.0]])]});
            extrude(context, id + "F30", {"entities" : qUnion([Q0]), "depth" : 60 * mm, "offsetDistance" : 25 * mm});
        }
        {
            var Q0;
            {var subQ5=sQuery(id+"F0.wireOp",EDGE,"E110");Q0=makeQuery(id+"F0.imprint","IMPRINT",FACE,{"disambiguationData":[TD([[makeQuery(id+"F0.imprint","IMPRINT",EDGE,{"derivedFrom":subQ5}),-1.0]])]});}
            var Q1;
            {var subQ1=sQuery(id+"F0.wireOp",EDGE,"E26");Q1=makeQuery(id+"F0.imprint","IMPRINT",FACE,{"disambiguationData":[TD([[makeQuery(id+"F0.imprint","IMPRINT",EDGE,{"derivedFrom":subQ1}),1.0]])]});}
            extrude(context, id + "F31", {"entities" : qUnion([Q0, Q1]), "depth" : 2400 * mm, "offsetDistance" : 25 * mm});
        }
        {
            var Q0;
            Q0=makeQuery(id+"F0.imprint","IMPRINT",FACE,{"disambiguationData":[TD([[makeQuery(id+"F0.imprint","IMPRINT",EDGE,{"derivedFrom":sQuery(id+"F0.wireOp",EDGE,"E116")}),1.0]])]});
            extrude(context, id + "F32", {"entities" : qUnion([Q0]), "depth" : 1000 * mm, "offsetDistance" : 25 * mm});
        }
    });
